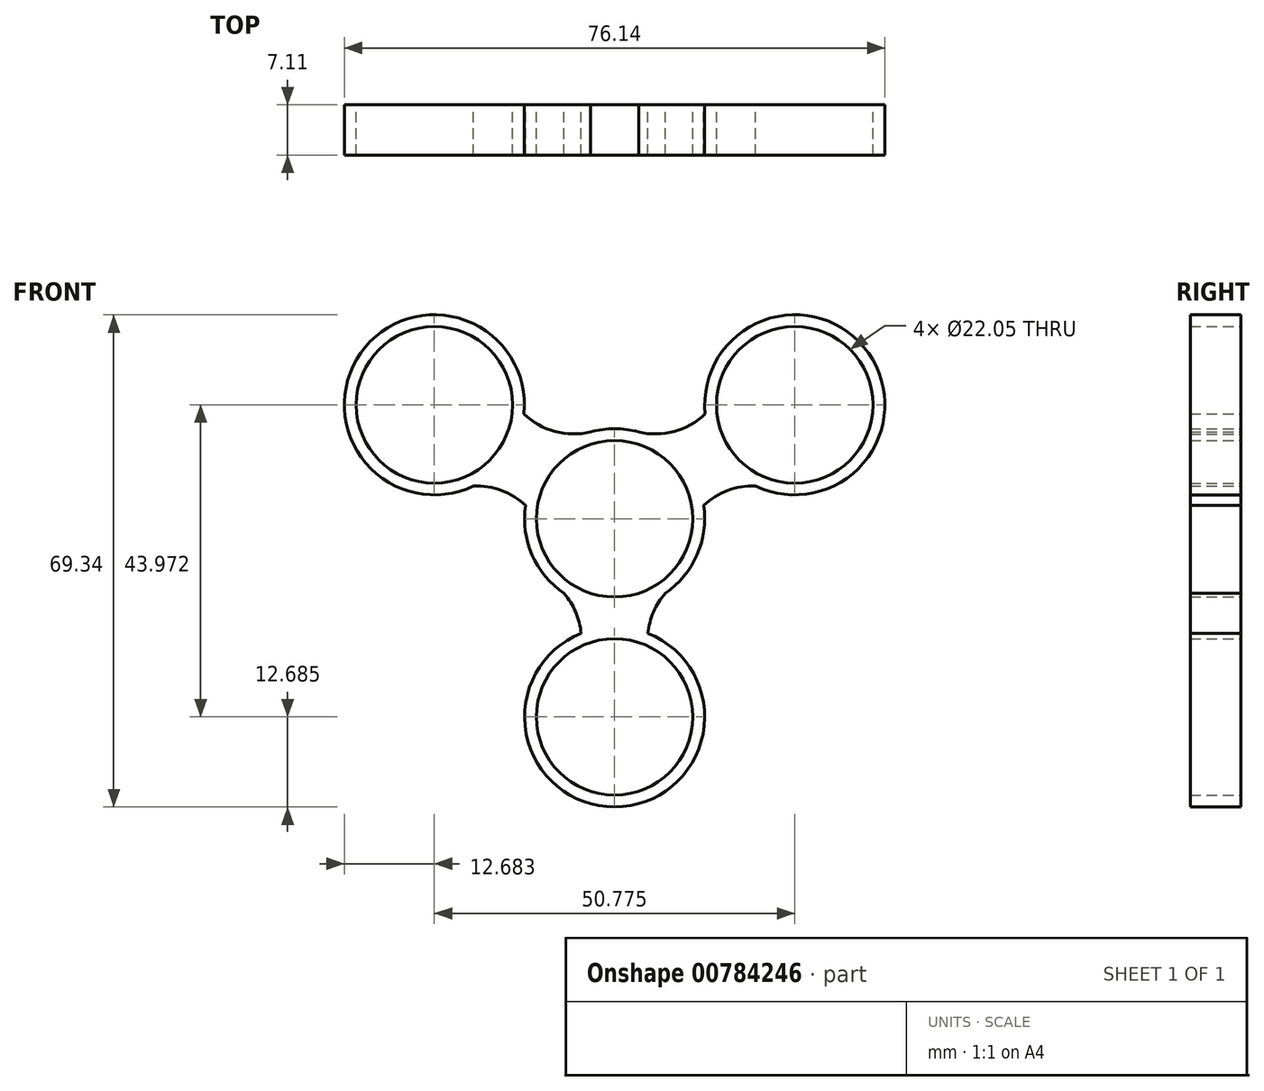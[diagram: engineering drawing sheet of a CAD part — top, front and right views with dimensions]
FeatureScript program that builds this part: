
annotation { "Feature Type Name" : "Feature", "Feature Type Description" : "" }
export const myFeature = defineFeature(function(context is Context, id is Id, definition is map)
    precondition{}
    {
        {
            var Q0;
            Q0=qCreatedBy(makeId("Front.planeOp"),FACE);
            var sketch = newSketch(context, id + "F0", { "sketchPlane" : qUnion([Q0])});
            skCircle(sketch, "E0", {"center": v(0, 0) * mm, "radius": 11.02 * mm});
            skCircle(sketch, "E1", {"center": v(0, 0) * mm, "radius": 12.69 * mm});
            skCircle(sketch, "E2", {"center": v(0, -27.91) * mm, "radius": 11.02 * mm});
            skCircle(sketch, "E3", {"center": v(0, -27.91) * mm, "radius": 12.69 * mm});
            skArc(sketch, "E4", {"start": v(7.13, -10.5) * mm, "mid": v(5.48, -13.13) * mm, "end": v(4.7, -16.13) * mm});
            skArc(sketch, "E5.MirrorCS", {"start": v(-7.13, -10.5) * mm, "mid": v(-5.48, -13.13) * mm, "end": v(-4.7, -16.13) * mm});
            skCircle(sketch, "E6", {"center": v(-25.39, 16.06) * mm, "radius": 11.02 * mm});
            skCircle(sketch, "E7", {"center": v(-25.39, 16.06) * mm, "radius": 12.69 * mm});
            skArc(sketch, "E8", {"start": v(-12.55, 1.87) * mm, "mid": v(-15.94, 3.98) * mm, "end": v(-19.88, 4.63) * mm});
            skArc(sketch, "E9.MirrorCS", {"start": v(-2.97, 12.33) * mm, "mid": v(-8.2, 12.26) * mm, "end": v(-12.77, 14.76) * mm});
            skArc(sketch, "E10.MirrorCS", {"start": v(2.97, 12.33) * mm, "mid": v(8.2, 12.26) * mm, "end": v(12.77, 14.76) * mm});
            skArc(sketch, "E11.MirrorCS", {"start": v(12.55, 1.87) * mm, "mid": v(15.94, 3.98) * mm, "end": v(19.88, 4.63) * mm});
            skCircle(sketch, "E12.MirrorC", {"center": v(25.39, 16.06) * mm, "radius": 12.69 * mm});
            skCircle(sketch, "E13.MirrorC", {"center": v(25.39, 16.06) * mm, "radius": 11.02 * mm});
            skLineSegment(sketch, "E14", {"start": v(-13.57, 7.5) * mm, "end": v(-13.41, 7.63) * mm});
            skLineSegment(sketch, "E15", {"start": v(-13.53, 9.75) * mm, "end": v(-13.55, 9.78) * mm});
            skLineSegment(sketch, "E16", {"start": v(-13.36, 9.88) * mm, "end": v(-13.38, 9.87) * mm});
            skLineSegment(sketch, "E17", {"start": v(-13.52, 7.02) * mm, "end": v(-13.54, 7.03) * mm});
            skLineSegment(sketch, "E18", {"start": v(-13.4, 7.65) * mm, "end": v(-13.42, 7.67) * mm});
            skLineSegment(sketch, "E19", {"start": v(-13.42, 7.67) * mm, "end": v(-13.56, 7.54) * mm});
            skSolve(sketch);
        }
        {
            var Q0;
            Q0=qSketchRegion(id+"F0",true);
            extrude(context, id + "F1", {"entities" : qUnion([Q0]), "depth" : 7.11 * mm, "offsetDistance" : 25.4 * mm});
        }
    });
